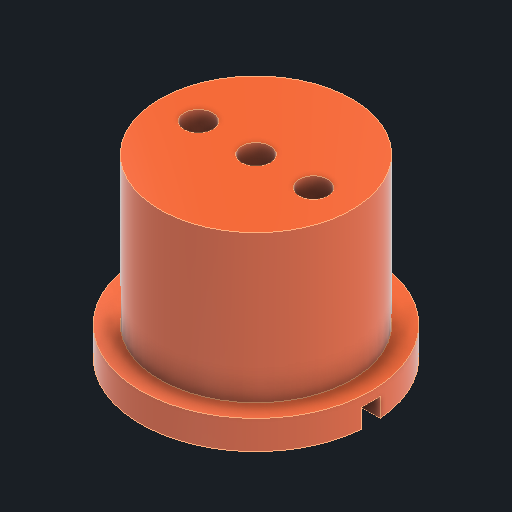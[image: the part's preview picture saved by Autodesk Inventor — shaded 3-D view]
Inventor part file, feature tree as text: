
AUTODESK INVENTOR PART (.ipt)
format: ipt  version: 2022 (Build 260153000, 153)  size: 170,496 bytes
history: native  units: mm
features: sketch x3, revolve x1, hole x1, extrude x1
ambient origin geometry x8: Origin, YZ Plane, XZ Plane, XY Plane, X Axis, Y Axis, Z Axis, Center Point
bodies: Solid1 (feature_tree)
feature tree (6):
  revolve  "Revolution1"  [1 undecoded]
  hole  "Hole1"  [1 undecoded]
  extrude  "Extrusion1"  Depth=2.0mm
  sketch  "Sketch1"  dims[d0=20.0mm d1=24.0mm]
  sketch  "Sketch2"  dims[d2=3.0mm d3=18.35mm]
  sketch  "Sketch3"  dims[d4=90.0deg d6=6.0mm d7=6.0mm d8=3.0mm d9=16.0mm d10=5.0mm d11=15.0mm d12=90.0deg d13=22.2mm d14=20.594885mm d15=30.0mm d16=2.0mm d17=2.0mm d18=0.0mm]
note: 2 required parameter values undecoded (feature->parameter linkage not recoverable at this tier; creation-order binding heuristic only, values carry confidence <= 0.55)